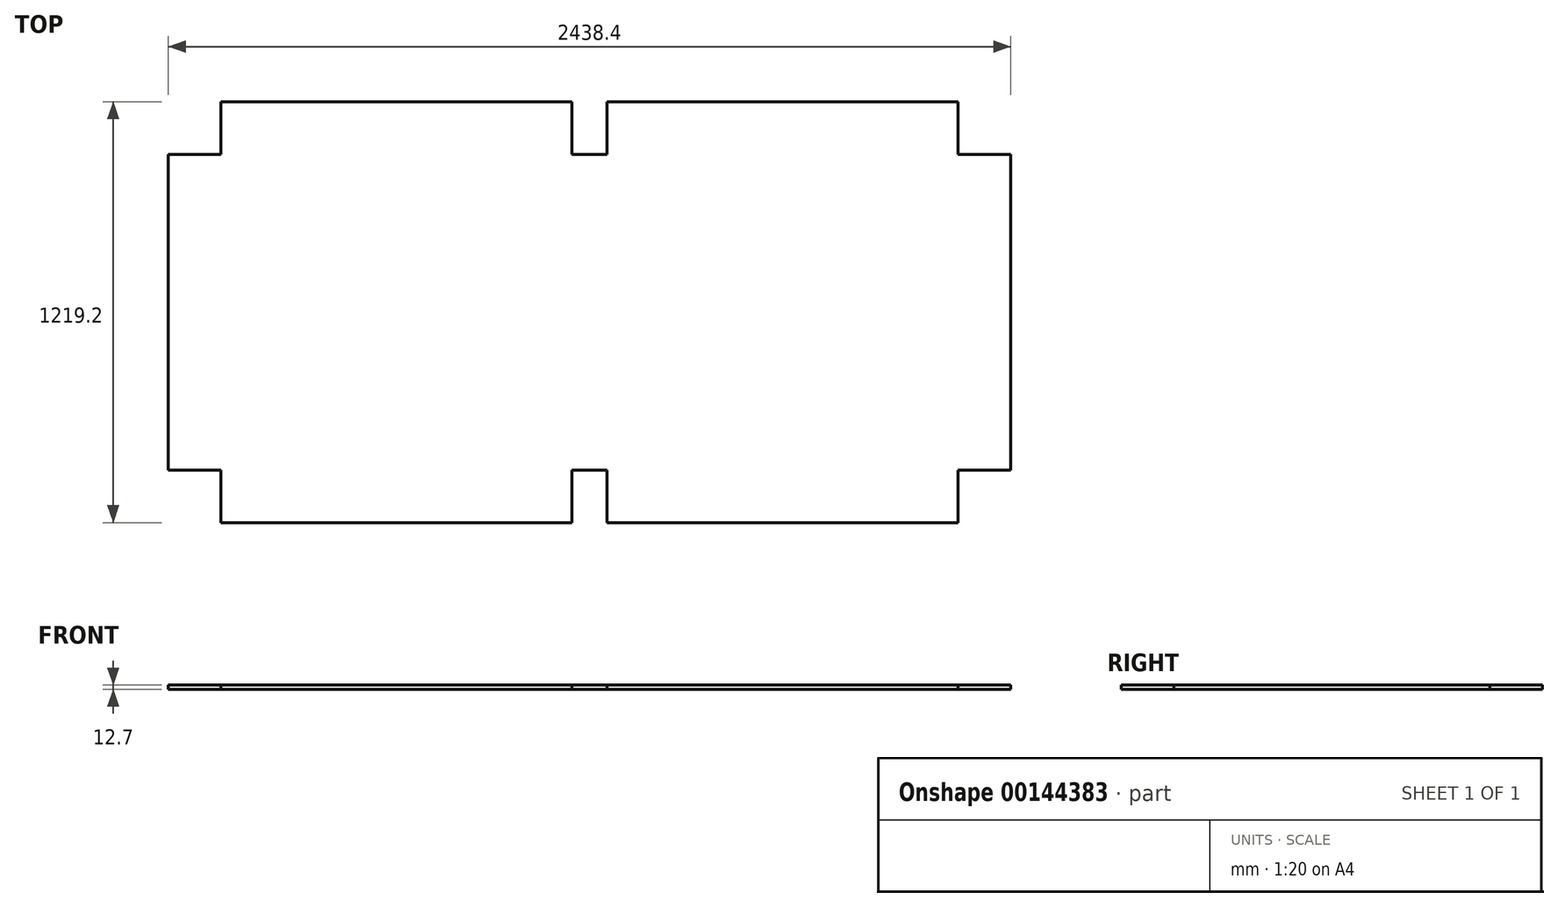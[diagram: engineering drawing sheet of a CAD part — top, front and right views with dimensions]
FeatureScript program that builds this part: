
annotation { "Feature Type Name" : "Feature", "Feature Type Description" : "" }
export const myFeature = defineFeature(function(context is Context, id is Id, definition is map)
    precondition{}
    {
        {
            var Q0;
            Q0=qCreatedBy(makeId("Top.planeOp"),FACE);
            var sketch = newSketch(context, id + "F0", { "sketchPlane" : qUnion([Q0])});
            skLineSegment(sketch, "E0.bottom", {"start": v(-1066.8, -609.6) * mm, "end": v(-50.8, -609.6) * mm});
            skLineSegment(sketch, "E0.top", {"start": v(-1066.8, 609.6) * mm, "end": v(-50.8, 609.6) * mm});
            skLineSegment(sketch, "E0.left", {"start": v(-1219.2, -457.2) * mm, "end": v(-1219.2, 457.2) * mm});
            skLineSegment(sketch, "E0.right", {"start": v(1219.2, -457.2) * mm, "end": v(1219.2, 457.2) * mm});
            skPoint(sketch, "E0.middle", {"position": v(0, 0) * mm});
            skLineSegment(sketch, "E1", {"start": v(-1066.8, 609.6) * mm, "end": v(-1066.8, 457.2) * mm});
            skLineSegment(sketch, "E2", {"start": v(-1066.8, 457.2) * mm, "end": v(-1219.2, 457.2) * mm});
            skPoint(sketch, "E3.orphan", {"position": v(-1219.2, 609.6) * mm});
            skLineSegment(sketch, "E4", {"start": v(-1219.2, -457.2) * mm, "end": v(-1066.8, -457.2) * mm});
            skLineSegment(sketch, "E5", {"start": v(-1066.8, -457.2) * mm, "end": v(-1066.8, -609.6) * mm});
            skPoint(sketch, "E6.orphan", {"position": v(-1219.2, -609.6) * mm});
            skLineSegment(sketch, "E7", {"start": v(0, 652.05) * mm, "end": v(0, -671.98) * mm, "construction": true});
            skLineSegment(sketch, "E8", {"start": v(-50.8, 609.6) * mm, "end": v(-50.8, 457.2) * mm});
            skLineSegment(sketch, "E9", {"start": v(-50.8, 457.2) * mm, "end": v(0, 457.2) * mm});
            skLineSegment(sketch, "E10.MirrorCS", {"start": v(50.8, 609.6) * mm, "end": v(50.8, 457.2) * mm});
            skLineSegment(sketch, "E11.MirrorCS", {"start": v(50.8, 457.2) * mm, "end": v(0, 457.2) * mm});
            skLineSegment(sketch, "E12.trimOffspring", {"start": v(50.8, 609.6) * mm, "end": v(1066.8, 609.6) * mm});
            skLineSegment(sketch, "E13", {"start": v(1066.8, 609.6) * mm, "end": v(1066.8, 457.2) * mm});
            skLineSegment(sketch, "E14", {"start": v(1066.8, 457.2) * mm, "end": v(1219.2, 457.2) * mm});
            skPoint(sketch, "E15.orphan", {"position": v(1219.2, 609.6) * mm});
            skLineSegment(sketch, "E16", {"start": v(1219.2, -457.2) * mm, "end": v(1066.8, -457.2) * mm});
            skLineSegment(sketch, "E17", {"start": v(1066.8, -457.2) * mm, "end": v(1066.8, -609.6) * mm});
            skLineSegment(sketch, "E18", {"start": v(-50.8, -609.6) * mm, "end": v(-50.8, -457.2) * mm});
            skLineSegment(sketch, "E19", {"start": v(-50.8, -457.2) * mm, "end": v(0, -457.2) * mm});
            skLineSegment(sketch, "E20.MirrorCS", {"start": v(50.8, -457.2) * mm, "end": v(0, -457.2) * mm});
            skLineSegment(sketch, "E21.MirrorCS", {"start": v(50.8, -609.6) * mm, "end": v(50.8, -457.2) * mm});
            skPoint(sketch, "E22.orphan", {"position": v(1219.2, -609.6) * mm});
            skLineSegment(sketch, "E23.trimOffspring", {"start": v(50.8, -609.6) * mm, "end": v(1066.8, -609.6) * mm});
            skSolve(sketch);
        }
        {
            var Q0;
            Q0=qCreatedBy(makeId("Top.planeOp"),FACE);
            var sketch = newSketch(context, id + "F1", { "sketchPlane" : qUnion([Q0])});
            skSolve(sketch);
        }
        {
            var Q0;
            Q0 = qSketchRegion(id + "F0", true);
            var Q1;
            Q1 = qSketchRegion(id + "F1", true);
            extrude(context, id + "F2", {"entities" : qUnion([Q0, Q1]), "depth" : 12.7 * mm});
        }
    });
